# Revit family: result
name_source: partatom
category: Plumbing Fixtures
revit_build: Autodesk Revit 2015 (Build: 20140903_1530(x64)
units: mm (PartAtom-declared; Revit-internal decimal feet)

## types (1)
- Default
    BIMobject category = Urinals
    BIMobject category code = sanitary-urinals
    BIMobject main category = Sanitary
    BIMobject main category code = sanitary
    Brand url = http://www.duravit.com
    Edition number = 1
    GTIN code = https://4063382018038
    IFC Classification = Sanitary Terminal
    Manufacturer name = DURAVIT
    Masterformat 2014 Code = 22 41 13.16
    Masterformat 2014 Description = Residential Urinals
    Material main = Ceramics
    NBS Reference Code = 31-93
    NBS Reference Description = Urinal And Wc Fittings
    OmniClass Code = 23-31 21 00
    OmniClass Description = Urinals
    Product Guid = 37d2ed62-0660-4760-ab58-b017cde97a6c
    Product SKU = white-tulip-urinal-281730
    Product data url = https://bimobject.com
    Product family = White Tulip
    Product group = Urinals
    Product name = 281730 Urinal
    Product url = https://duravit-public-assets.s3.eu-central-1.amazonaws.com
    QR code = http://bimobject.com
    UNSPSC Code = 30181506
    Uniclass 1.4 Code = L721
    Uniclass 1.4 Description = Sanitary equipment
    Uniclass 2.0 Code = PR-31-93
    Uniclass 2.0 Description = Urinal And Wc Fittings
    Uniclass 2015 Code = Pr_40_20_93
    Uniclass 2015 Name = Urinal and WC fittings
    Uniformat II Code = D2010
    Uniformat II Description = Plumbing Fixtures

## geometry (parser evidence)
native form markers: Sweep x3
no freeform markers — native parametric forms only
